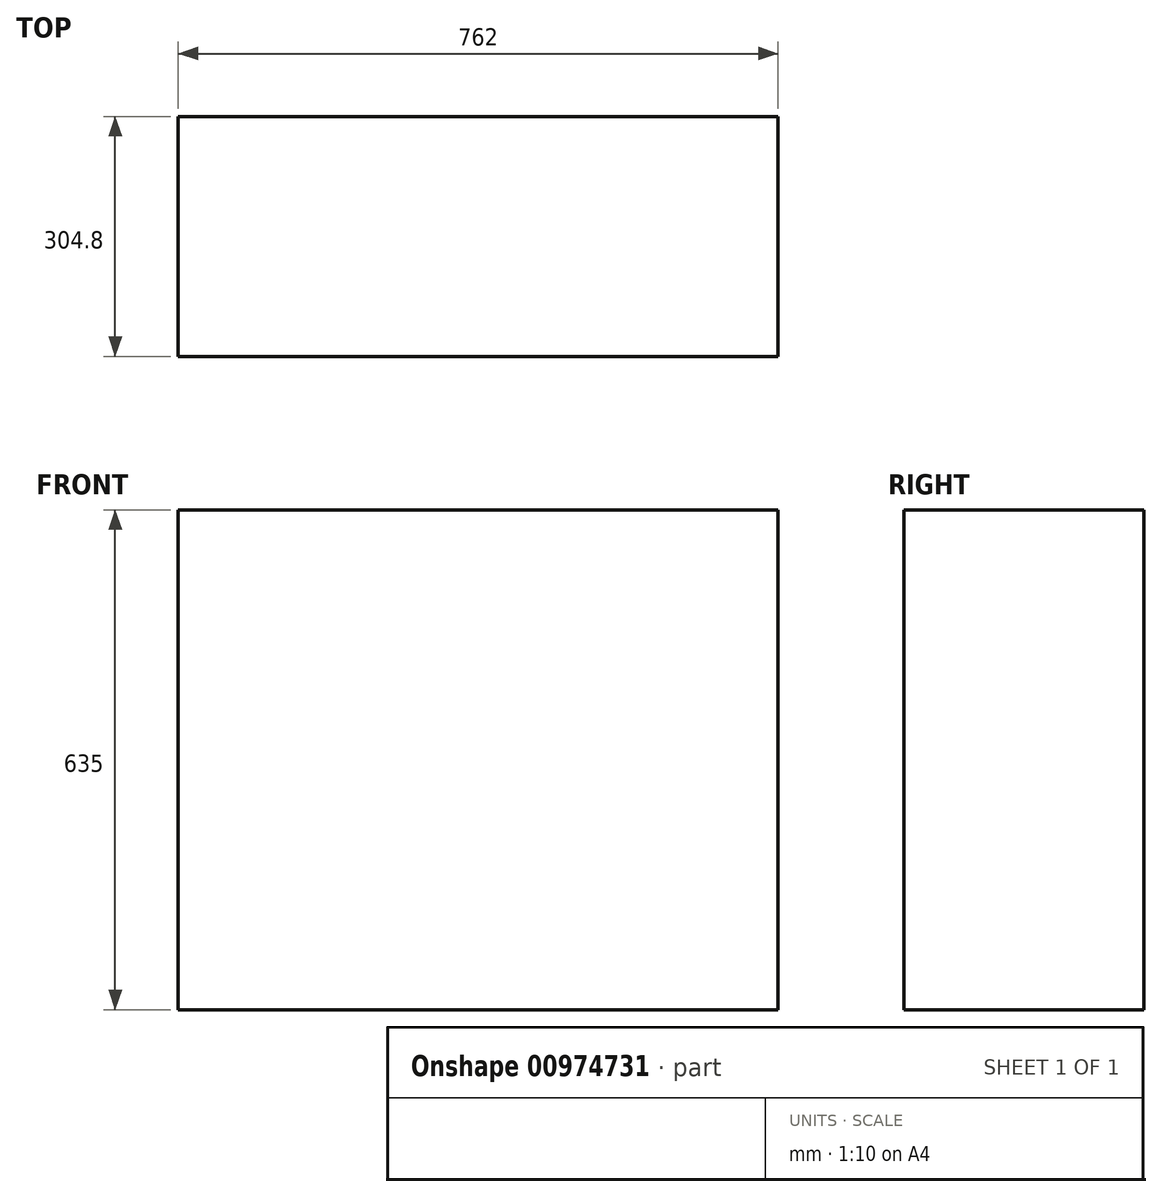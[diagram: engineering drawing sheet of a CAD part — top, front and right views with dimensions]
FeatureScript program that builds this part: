
annotation { "Feature Type Name" : "Feature", "Feature Type Description" : "" }
export const myFeature = defineFeature(function(context is Context, id is Id, definition is map)
    precondition{}
    {
        {
            var Q0;
            Q0=qCreatedBy(makeId("Front.planeOp"),FACE);
            var sketch = newSketch(context, id + "F0", { "sketchPlane" : qUnion([Q0])});
            skLineSegment(sketch, "E0.bottom", {"start": v(-350.57, 25.21) * mm, "end": v(411.43, 25.21) * mm});
            skLineSegment(sketch, "E0.top", {"start": v(-350.57, -609.79) * mm, "end": v(411.43, -609.79) * mm});
            skLineSegment(sketch, "E0.left", {"start": v(-350.57, 25.21) * mm, "end": v(-350.57, -609.79) * mm});
            skLineSegment(sketch, "E0.right", {"start": v(411.43, 25.21) * mm, "end": v(411.43, -609.79) * mm});
            skSolve(sketch);
        }
        {
            var Q0;
            Q0=makeQuery(id+"F0.imprint","IMPRINT",FACE,{"disambiguationData":[TD([[makeQuery(id+"F0.imprint","IMPRINT",EDGE,{"derivedFrom":sQuery(id+"F0.wireOp",EDGE,"E0.bottom")}),-1.0]])]});
            extrude(context, id + "F1", {"entities" : qUnion([Q0]), "depth" : 304.8 * mm, "offsetDistance" : 25.4 * mm});
        }
    });
